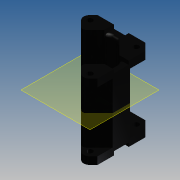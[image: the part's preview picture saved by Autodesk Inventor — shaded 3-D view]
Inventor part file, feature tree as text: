
AUTODESK INVENTOR PART (.ipt)
format: ipt  version: 2013 (Build 170138000, 138)  size: 315,392 bytes
history: native  units: mm
features: extrude x6, sketch x6, fillet x4, projected_geometry x4, chamfer x1, plane x1, mirror x1
ambient origin geometry x8: Origin, YZ Plane, XZ Plane, XY Plane, X Axis, Y Axis, Z Axis, Center Point
bodies: Solid1 (feature_tree)
feature tree (23):
  extrude  "Extrusion1"  Depth=42.0mm
  extrude  "Extrusion2"  Depth=3.5mm
  extrude  "Extrusion3"  Depth=5.0mm
  extrude  "Extrusion4"  Depth=5.0mm
  chamfer  "Chamfer1"  Distance=5.0mm
  fillet  "Fillet3"  Radius=5.0mm
  extrude  "Extrusion5"  Depth=3.0mm
  plane  "Work Plane1"
  mirror  "Mirror1"
  fillet  "Fillet4"  Radius=40.0mm
  extrude  "Extrusion6"  Depth=40.0mm TaperAngle=0.0deg
  fillet  "Fillet5"  Radius=5.0mm
  fillet  "Fillet6"  Radius=5.0mm
  sketch  "Sketch1"  dims[d0=31.0mm d1=42.0mm]
  sketch  "Sketch2"  dims[d2=22.5mm d3=3.5mm]
  sketch  "Sketch3"  dims[d4=5.0mm d5=0.0mm d6=5.0mm]
  sketch  "Sketch4"  dims[d8=3.0mm d9=5.0mm]
  projected_geometry  "Projected Loop1"
  projected_geometry  "Projected Loop2"
  projected_geometry  "Projected Loop3"
  sketch  "Sketch5"  dims[d10=3.0mm]
  sketch  "Sketch6"  dims[d11=45.0deg d12=5.0mm d13=5.0mm d14=3.0mm d15=40.0mm d16=0.0mm d17=40.0mm d18=0.0mm d19=5.0mm d20=0.0mm d23=5.0mm d24=2.0mm d25=45.0deg d26=5.5mm d27=10.0mm d29=2.5mm d30=0.0mm d31=2.5mm d32=4.243mm d33=2.5mm d34=0.0mm d35=4.24mm d36=2.5mm]
  projected_geometry  "Projected Loop4"
